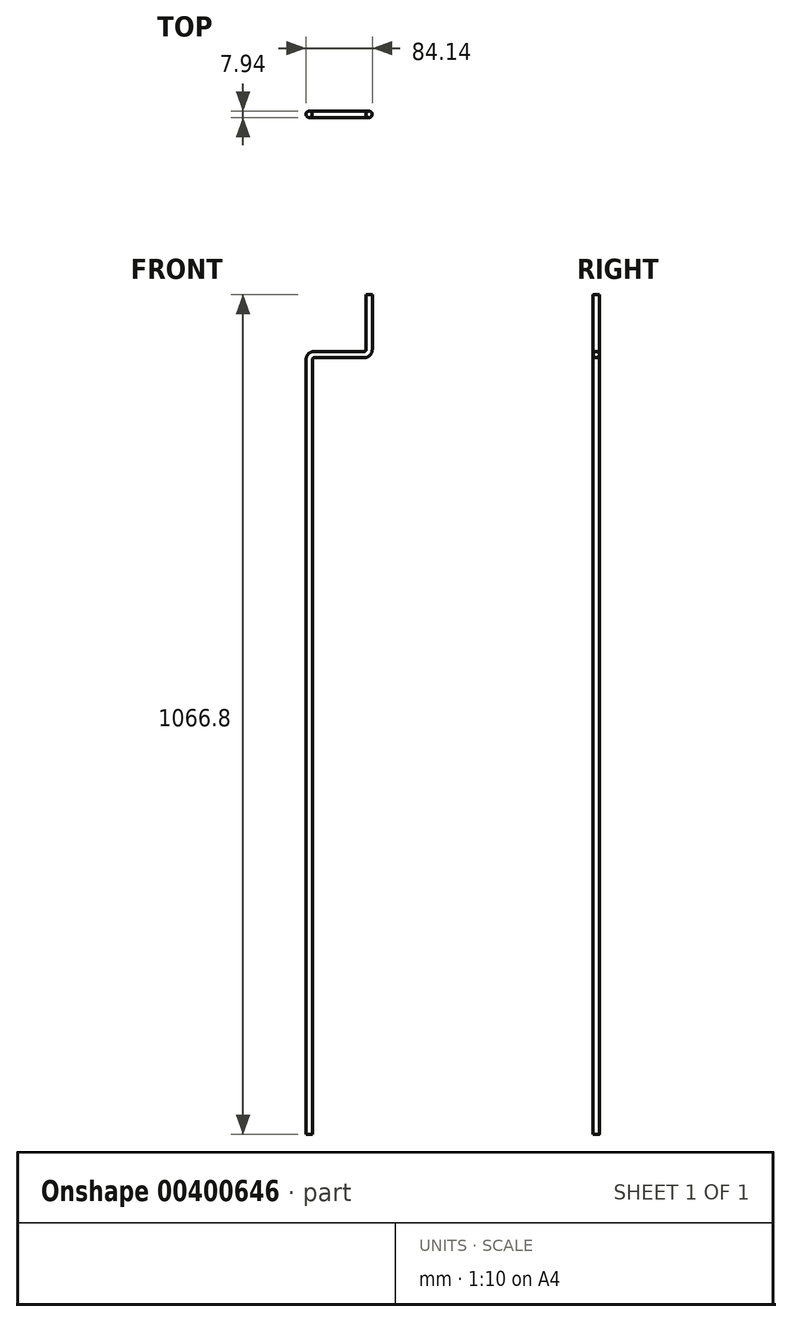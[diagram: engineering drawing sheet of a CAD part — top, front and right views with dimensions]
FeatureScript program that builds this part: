
annotation { "Feature Type Name" : "Feature", "Feature Type Description" : "" }
export const myFeature = defineFeature(function(context is Context, id is Id, definition is map)
    precondition{}
    {
        {
            var Q0;
            Q0=qCreatedBy(makeId("Front.planeOp"),FACE);
            var sketch = newSketch(context, id + "F0", { "sketchPlane" : qUnion([Q0])});
            skLineSegment(sketch, "E0", {"start": v(-76.2, -1066.8) * mm, "end": v(-76.2, -82.55) * mm});
            skLineSegment(sketch, "E1", {"start": v(-69.85, -76.2) * mm, "end": v(-6.35, -76.2) * mm});
            skLineSegment(sketch, "E2", {"start": v(0, -69.85) * mm, "end": v(0, 0) * mm});
            skPoint(sketch, "E3.visualSharp", {"position": v(0, -76.2) * mm});
            skArc(sketch, "E3.filletArc", {"start": v(-6.35, -76.2) * mm, "mid": v(-1.86, -74.34) * mm, "end": v(0, -69.85) * mm});
            skPoint(sketch, "E4.visualSharp", {"position": v(-76.2, -76.2) * mm});
            skArc(sketch, "E4.filletArc", {"start": v(-69.85, -76.2) * mm, "mid": v(-74.34, -78.06) * mm, "end": v(-76.2, -82.55) * mm});
            skSolve(sketch);
        }
        {
            var Q0;
            Q0=qCreatedBy(makeId("Top.planeOp"),FACE);
            var sketch = newSketch(context, id + "F1", { "sketchPlane" : qUnion([Q0])});
            skCircle(sketch, "E5", {"center": v(0, 0) * mm, "radius": 3.97 * mm});
            skSolve(sketch);
        }
        {
            var Q0;
            Q0=makeQuery(id+"F1.imprint","IMPRINT",FACE,{"disambiguationData":[TD([[makeQuery(id+"F1.imprint","IMPRINT",EDGE,{"derivedFrom":sQuery(id+"F1.wireOp",EDGE,"E5")}),1.0]])]});
            var Q1;
            Q1 = qConstructionFilter(qBodyType(qCreatedBy(id + "F0" ,EDGE), BodyType.WIRE), ConstructionObject.NO);
            sweep(context, id + "F2", {"profiles" : qUnion([Q0]), "path" : qUnion([Q1])});
        }
    });
